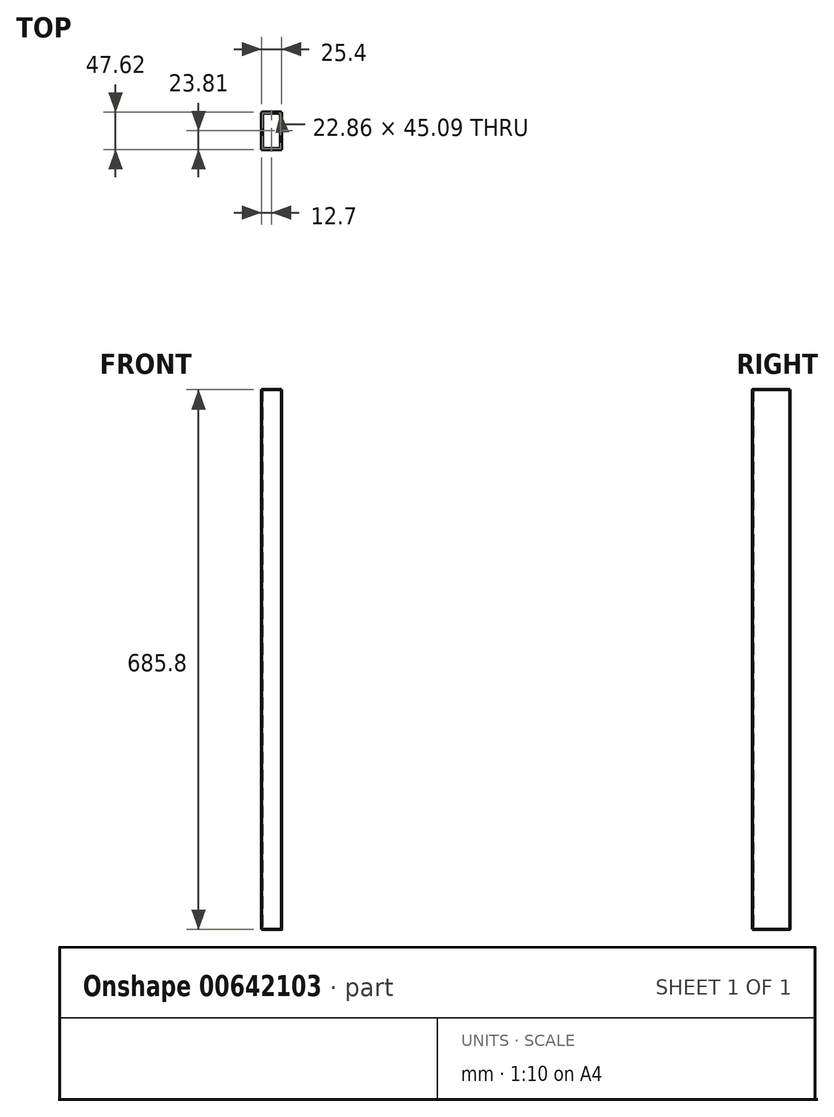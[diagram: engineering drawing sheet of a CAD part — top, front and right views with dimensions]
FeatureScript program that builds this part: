
annotation { "Feature Type Name" : "Feature", "Feature Type Description" : "" }
export const myFeature = defineFeature(function(context is Context, id is Id, definition is map)
    precondition{}
    {
        {
            var Q0;
            Q0=qCreatedBy(makeId("Top.planeOp"),FACE);
            var sketch = newSketch(context, id + "F0", { "sketchPlane" : qUnion([Q0])});
            skLineSegment(sketch, "E0.bottom", {"start": v(12.07, -23.81) * mm, "end": v(-12.07, -23.81) * mm});
            skLineSegment(sketch, "E0.top", {"start": v(12.06, 23.81) * mm, "end": v(-11.43, 23.81) * mm});
            skLineSegment(sketch, "E0.left", {"start": v(12.7, -23.18) * mm, "end": v(12.7, 23.18) * mm});
            skLineSegment(sketch, "E0.right", {"start": v(-12.7, -23.18) * mm, "end": v(-12.7, 22.54) * mm});
            skPoint(sketch, "E0.middle", {"position": v(0, 0) * mm});
            skPoint(sketch, "E1.visualSharp", {"position": v(-12.7, 23.81) * mm});
            skArc(sketch, "E1.filletArc", {"start": v(-11.43, 23.81) * mm, "mid": v(-12.33, 23.44) * mm, "end": v(-12.7, 22.54) * mm});
            skPoint(sketch, "E2.visualSharp", {"position": v(12.7, 23.81) * mm});
            skArc(sketch, "E2.filletArc", {"start": v(12.7, 23.18) * mm, "mid": v(12.51, 23.63) * mm, "end": v(12.06, 23.81) * mm});
            skPoint(sketch, "E3.visualSharp", {"position": v(-12.7, -23.81) * mm});
            skArc(sketch, "E3.filletArc", {"start": v(-12.7, -23.18) * mm, "mid": v(-12.51, -23.63) * mm, "end": v(-12.07, -23.81) * mm});
            skPoint(sketch, "E4.visualSharp", {"position": v(12.7, -23.81) * mm});
            skArc(sketch, "E4.filletArc", {"start": v(12.07, -23.81) * mm, "mid": v(12.51, -23.63) * mm, "end": v(12.7, -23.18) * mm});
            skLineSegment(sketch, "E5.bottom", {"start": v(-11.43, 22.54) * mm, "end": v(11.43, 22.54) * mm});
            skLineSegment(sketch, "E5.top", {"start": v(-11.43, -22.54) * mm, "end": v(11.43, -22.54) * mm});
            skLineSegment(sketch, "E5.left", {"start": v(-11.43, 22.54) * mm, "end": v(-11.43, -22.54) * mm});
            skLineSegment(sketch, "E5.right", {"start": v(11.43, 22.54) * mm, "end": v(11.43, -22.54) * mm});
            skSolve(sketch);
        }
        {
            var Q0;
            Q0=makeQuery(id+"F0.imprint","IMPRINT",FACE,{"disambiguationData":[TD([[makeQuery(id+"F0.imprint","IMPRINT",EDGE,{"derivedFrom":sQuery(id+"F0.wireOp",EDGE,"E0.bottom")}),-1.0]])]});
            extrude(context, id + "F1", {"entities" : qUnion([Q0]), "depth" : 685.8 * mm, "offsetDistance" : 25.4 * mm});
        }
    });
